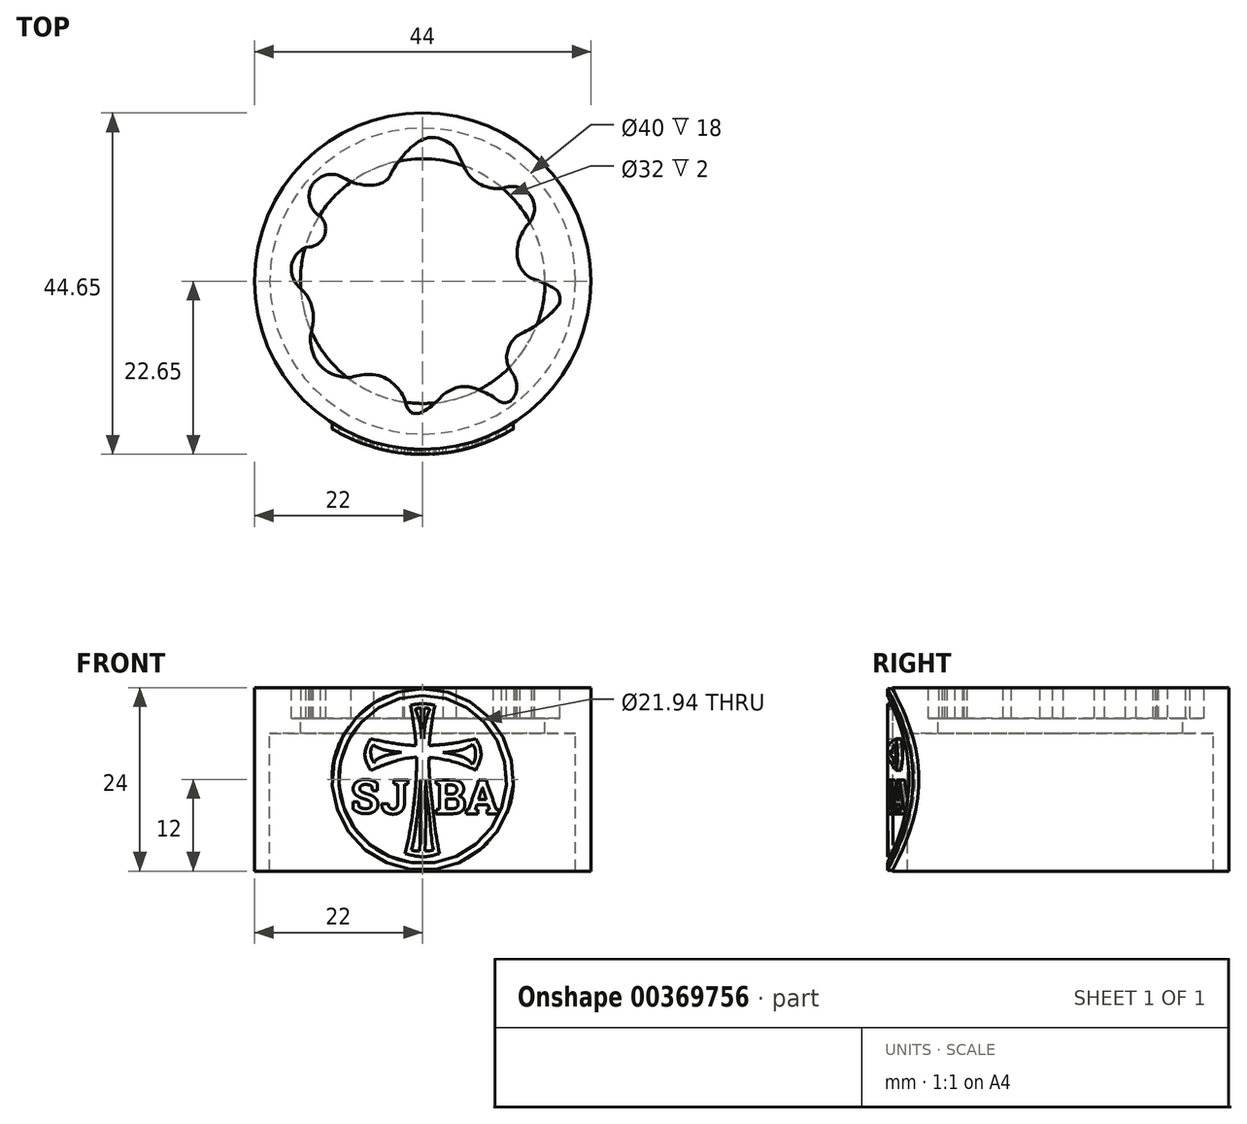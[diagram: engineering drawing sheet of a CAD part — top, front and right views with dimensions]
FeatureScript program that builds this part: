
annotation { "Feature Type Name" : "Feature", "Feature Type Description" : "" }
export const myFeature = defineFeature(function(context is Context, id is Id, definition is map)
    precondition{}
    {
        {
            var Q0;
            Q0=qCreatedBy(makeId("Top.planeOp"),FACE);
            var Q1;
            Q1=qBodyType(qCreatedBy(id+"F1",EDGE),BodyType.WIRE);
            cPlane(context, id + "F0", {"entities" : qUnion([Q0, Q1]), "cplaneType" : CPlaneType.OFFSET, "offset" : 12 * mm, "width" : 150 * mm, "height" : 150 * mm});
        }
        {
            var Q0;
            Q0=qCreatedBy(id+"F0.planeOp",FACE);
            var sketch = newSketch(context, id + "F1", { "sketchPlane" : qUnion([Q0])});
            skCircle(sketch, "E0", {"center": v(0, 0) * mm, "radius": 22 * mm});
            skFitSpline(sketch, "E1", {"points": [v(-14.3, 12.84) * mm, v(-11.44, 13.95) * mm, v(-6.4, 12.53) * mm], "startDerivative": vector(4.46, 5.6) * mm, "endDerivative": vector(16.32, 0.58) * mm});
            skFitSpline(sketch, "E2", {"points": [v(-14.3, 12.84) * mm, v(-14.8, 10.36) * mm, v(-13.38, 8.48) * mm], "startDerivative": vector(-2.91, -3.74) * mm, "endDerivative": vector(4.44, -2.3) * mm});
            skFitSpline(sketch, "E3", {"points": [v(-13.38, 8.48) * mm, v(-12.7, 6.62) * mm, v(-15.26, 4.45) * mm], "startDerivative": vector(2.5, -2.67) * mm, "endDerivative": vector(-9.07, 0.1) * mm});
            skFitSpline(sketch, "E4", {"points": [v(-15.26, 4.45) * mm, v(-17.17, 1.96) * mm, v(-15.87, -1.05) * mm], "startDerivative": vector(-5.88, -2.54) * mm, "endDerivative": vector(5.37, -3.99) * mm});
            skFitSpline(sketch, "E5", {"points": [v(-15.87, -1.05) * mm, v(-14.36, -3.98) * mm, v(-14.54, -6.45) * mm], "startDerivative": vector(4.6, -4.23) * mm, "endDerivative": vector(-1.12, -5.28) * mm});
            skFitSpline(sketch, "E6", {"points": [v(-14.54, -6.45) * mm, v(-14.3, -9.6) * mm, v(-9.38, -12.57) * mm], "startDerivative": vector(-1.49, -4.88) * mm, "endDerivative": vector(14.07, 0.6) * mm});
            skFitSpline(sketch, "E7", {"points": [v(-9.38, -12.57) * mm, v(-5.16, -12.57) * mm, v(-2.36, -15.43) * mm], "startDerivative": vector(7.18, 2.12) * mm, "endDerivative": vector(2.53, -6.19) * mm});
            skFitSpline(sketch, "E8", {"points": [v(-2.36, -15.43) * mm, v(-0.75, -17.32) * mm, v(2.7, -14.82) * mm], "startDerivative": vector(1.67, -9.42) * mm, "endDerivative": vector(5.03, 5.85) * mm});
            skFitSpline(sketch, "E9", {"points": [v(2.7, -14.82) * mm, v(5.45, -13.78) * mm, v(9.22, -15.14) * mm], "startDerivative": vector(4.06, 3.24) * mm, "endDerivative": vector(7.18, -3.93) * mm});
            skFitSpline(sketch, "E10", {"points": [v(9.22, -15.14) * mm, v(11.11, -15.85) * mm, v(12.13, -12.78) * mm], "startDerivative": vector(4.38, -3.77) * mm, "endDerivative": vector(-2.9, 8.35) * mm});
            skFitSpline(sketch, "E11", {"points": [v(12.13, -12.78) * mm, v(11.06, -10.66) * mm, v(11.96, -7.51) * mm], "startDerivative": vector(-1.65, 4.16) * mm, "endDerivative": vector(4.57, 5.25) * mm});
            skFitSpline(sketch, "E12", {"points": [v(11.96, -7.51) * mm, v(14.65, -5.88) * mm, v(17.91, -2.7) * mm], "startDerivative": vector(3.62, 3.57) * mm, "endDerivative": vector(-0.15, 3.1) * mm});
            skFitSpline(sketch, "E13", {"points": [v(17.91, -2.7) * mm, v(16.74, -0.7) * mm, v(14.28, 0.37) * mm], "startDerivative": vector(0.98, 7.59) * mm, "endDerivative": vector(-4.1, 1.2) * mm});
            skFitSpline(sketch, "E14", {"points": [v(14.28, 0.37) * mm, v(12.43, 2.83) * mm, v(12.74, 5.73) * mm], "startDerivative": vector(-6.41, 2.8) * mm, "endDerivative": vector(2.08, 5.38) * mm});
            skFitSpline(sketch, "E15", {"points": [v(12.74, 5.73) * mm, v(14.05, 7.73) * mm, v(14.57, 9.89) * mm], "startDerivative": vector(4.72, 10.1) * mm, "endDerivative": vector(-1.17, 4.74) * mm});
            skFitSpline(sketch, "E16", {"points": [v(14.57, 9.89) * mm, v(13.17, 12.02) * mm, v(10.32, 12.08) * mm], "startDerivative": vector(0.08, 3.85) * mm, "endDerivative": vector(-4.12, -2.28) * mm});
            skFitSpline(sketch, "E17", {"points": [v(10.32, 12.08) * mm, v(6.46, 13.4) * mm, v(4.44, 16.97) * mm], "startDerivative": vector(-9.93, -0.41) * mm, "endDerivative": vector(-5.62, 10.83) * mm});
            skFitSpline(sketch, "E18", {"points": [v(4.44, 16.97) * mm, v(1.52, 18.8) * mm, v(-2.58, 16.4) * mm], "startDerivative": vector(-2.9, 6.35) * mm, "endDerivative": vector(-8.38, -9.56) * mm});
            skFitSpline(sketch, "E19", {"points": [v(-2.58, 16.4) * mm, v(-4.36, 13.61) * mm, v(-6.4, 12.53) * mm], "startDerivative": vector(-9.43, -11.95) * mm, "endDerivative": vector(-8.2, -1.4) * mm});
            skCircle(sketch, "E20", {"center": v(0, 0) * mm, "radius": 20 * mm});
            skSolve(sketch);
        }
        {
            var Q0;
            Q0=qCreatedBy(makeId("Top.planeOp"),FACE);
            cPlane(context, id + "F2", {"entities" : qUnion([Q0]), "cplaneType" : CPlaneType.OFFSET, "offset" : 8 * mm, "width" : 150 * mm, "height" : 150 * mm});
        }
        {
            var Q0;
            Q0=qCreatedBy(id+"F2.planeOp",FACE);
            var sketch = newSketch(context, id + "F3", { "sketchPlane" : qUnion([Q0])});
            skCircle(sketch, "E21", {"center": v(0, 0) * mm, "radius": 20 * mm});
            skCircle(sketch, "E22", {"center": v(0, 0) * mm, "radius": 16 * mm});
            skSolve(sketch);
        }
        {
            var Q0;
            Q0=makeQuery(id+"F1.imprint","IMPRINT",FACE,{"disambiguationData":[TD([[makeQuery(id+"F1.imprint","IMPRINT",EDGE,{"derivedFrom":sQuery(id+"F1.wireOp",EDGE,"E1")}),1.0]])]});
            extrude(context, id + "F4", {"entities" : qUnion([Q0]), "oppositeDirection" : true, "depth" : 4 * mm});
        }
        {
            var Q0;
            Q0=makeQuery(id+"F1.imprint","IMPRINT",FACE,{"disambiguationData":[TD([[makeQuery(id+"F1.imprint","IMPRINT",EDGE,{"derivedFrom":sQuery(id+"F1.wireOp",EDGE,"E0")}),1.0]])]});
            extrude(context, id + "F5", {"entities" : qUnion([Q0]), "operationType" : NewBodyOperationType.ADD, "oppositeDirection" : true, "depth" : 24 * mm});
        }
        {
            var Q0;
            Q0=makeQuery(id+"F3.imprint","IMPRINT",FACE,{"disambiguationData":[TD([[makeQuery(id+"F3.imprint","IMPRINT",EDGE,{"derivedFrom":sQuery(id+"F3.wireOp",EDGE,"E21")}),1.0]])]});
            extrude(context, id + "F6", {"entities" : qUnion([Q0]), "operationType" : NewBodyOperationType.ADD, "oppositeDirection" : true, "depth" : 2 * mm});
        }
        {
            var Q0;
            Q0=qCreatedBy(id+"F0.planeOp",FACE);
            var sketch = newSketch(context, id + "F7", { "sketchPlane" : qUnion([Q0])});
            skCircle(sketch, "E23", {"center": v(0, 0) * mm, "radius": 22.65 * mm});
            skSolve(sketch);
        }
        {
            var Q0;
            Q0=qSketchRegion(id+"F7",true);
            var Q1;
            Q1=qConstructionFilter(qBodyType(qCreatedBy(id+"F7",EDGE),BodyType.WIRE),ConstructionObject.NO);
            extrude(context, id + "F8", {"entities" : qUnion([Q0]), "bodyType" : ToolBodyType.SURFACE, "operationType" : NewBodyOperationType.ADD, "surfaceEntities" : qUnion([Q1]), "oppositeDirection" : true, "depth" : 24 * mm});
        }
        {
            var Q0;
            Q0=qCreatedBy(makeId("Front.planeOp"),FACE);
            var sketch = newSketch(context, id + "F9", { "sketchPlane" : qUnion([Q0])});
            skCircle(sketch, "E24", {"center": v(0, 0) * mm, "radius": 11.87 * mm});
            skCircle(sketch, "E25", {"center": v(0, 0) * mm, "radius": 10.97 * mm});
            skFitSpline(sketch, "E26", {"points": [v(-1.6, 9.68) * mm, v(0, 9.89) * mm, v(1.61, 9.69) * mm], "startDerivative": vector(3.27, 0.75) * mm, "endDerivative": vector(4.3, -0.93) * mm});
            skFitSpline(sketch, "E27", {"points": [v(-0.95, 9.2) * mm, v(-0.62, 9.29) * mm, v(-0.24, 9.32) * mm], "startDerivative": vector(1.32, 0.5) * mm, "endDerivative": vector(1.3, -0.13) * mm});
            skFitSpline(sketch, "E28", {"points": [v(0.2, 9.33) * mm, v(0.57, 9.3) * mm, v(0.92, 9.18) * mm], "startDerivative": vector(0.76, -0.01) * mm, "endDerivative": vector(0.68, -0.27) * mm});
            skFitSpline(sketch, "E29", {"points": [v(-0.95, 9.2) * mm, v(-0.35, 7.32) * mm, v(-0.14, 5.33) * mm], "startDerivative": vector(1.4, -3.74) * mm, "endDerivative": vector(0.22, -4.02) * mm});
            skFitSpline(sketch, "E30", {"points": [v(-0.24, 9.32) * mm, v(-0.14, 7.25) * mm, v(-0.14, 5.33) * mm], "startDerivative": vector(0.55, -4.52) * mm, "endDerivative": vector(-0.28, -3.72) * mm});
            skFitSpline(sketch, "E31", {"points": [v(0.2, 9.33) * mm, v(0.11, 7.22) * mm, v(0.13, 5.32) * mm], "startDerivative": vector(-0.59, -4.52) * mm, "endDerivative": vector(0.33, -3.76) * mm});
            skFitSpline(sketch, "E32", {"points": [v(0.92, 9.18) * mm, v(0.34, 7.3) * mm, v(0.13, 5.32) * mm], "startDerivative": vector(-1.38, -3.36) * mm, "endDerivative": vector(-0.21, -3.99) * mm});
            skFitSpline(sketch, "E33", {"points": [v(-1.6, 9.68) * mm, v(-1.16, 7) * mm, v(-0.9, 4.42) * mm], "startDerivative": vector(1.25, -5.72) * mm, "endDerivative": vector(0.17, -4.96) * mm});
            skFitSpline(sketch, "E34", {"points": [v(1.61, 9.69) * mm, v(1.1, 6.86) * mm, v(0.85, 4.42) * mm], "startDerivative": vector(-1.57, -6.3) * mm, "endDerivative": vector(-0.19, -5) * mm});
            skFitSpline(sketch, "E35", {"points": [v(0.85, 4.42) * mm, v(3.78, 4.7) * mm, v(6.94, 5.32) * mm], "startDerivative": vector(5.94, 0.4) * mm, "endDerivative": vector(6.24, 1.38) * mm});
            skFitSpline(sketch, "E36", {"points": [v(6.94, 5.32) * mm, v(7.64, 3.38) * mm, v(6.94, 1.21) * mm], "startDerivative": vector(2.1, -3.9) * mm, "endDerivative": vector(-2.07, -4.3) * mm});
            skFitSpline(sketch, "E37", {"points": [v(6.94, 1.21) * mm, v(3.65, 2.41) * mm, v(0.84, 2.9) * mm], "startDerivative": vector(-6.35, 2.62) * mm, "endDerivative": vector(-5.85, 0.72) * mm});
            skFitSpline(sketch, "E38", {"points": [v(-0.9, 4.42) * mm, v(-3.84, 4.73) * mm, v(-6.81, 5.3) * mm], "startDerivative": vector(-6.82, 0.08) * mm, "endDerivative": vector(-5.92, 1.3) * mm});
            skFitSpline(sketch, "E39", {"points": [v(-6.81, 5.3) * mm, v(-7.57, 3.31) * mm, v(-6.81, 1.17) * mm], "startDerivative": vector(-2.27, -4.02) * mm, "endDerivative": vector(2.25, -4.25) * mm});
            skFitSpline(sketch, "E40", {"points": [v(-6.81, 1.17) * mm, v(-3.87, 2.3) * mm, v(-0.79, 2.9) * mm], "startDerivative": vector(5.8, 2.52) * mm, "endDerivative": vector(6.2, 0.13) * mm});
            skFitSpline(sketch, "E41", {"points": [v(-0.79, 2.9) * mm, v(-1.18, -3.52) * mm, v(-2.3, -9.7) * mm], "startDerivative": vector(0.03, -12.8) * mm, "endDerivative": vector(-3.05, -12.4) * mm});
            skFitSpline(sketch, "E42", {"points": [v(0.84, 2.9) * mm, v(1.3, -3.5) * mm, v(2.2, -9.72) * mm], "startDerivative": vector(-0.69, -12.85) * mm, "endDerivative": vector(2.87, -12.23) * mm});
            skFitSpline(sketch, "E43", {"points": [v(-2.3, -9.7) * mm, v(0, -10.11) * mm, v(2.2, -9.72) * mm], "startDerivative": vector(4.57, -1.2) * mm, "endDerivative": vector(4.44, 1.2) * mm});
            skFitSpline(sketch, "E44", {"points": [v(-0.31, -0.15) * mm, v(-0.77, -5.17) * mm, v(-1.46, -9.24) * mm], "startDerivative": vector(-0.44, -9.93) * mm, "endDerivative": vector(-2.1, -8.23) * mm});
            skFitSpline(sketch, "E45", {"points": [v(-0.31, -0.15) * mm, v(-0.31, -5.21) * mm, v(-0.4, -9.39) * mm], "startDerivative": vector(0.34, -10.34) * mm, "endDerivative": vector(-0.5, -8.7) * mm});
            skFitSpline(sketch, "E46", {"points": [v(-1.46, -9.24) * mm, v(-0.92, -9.37) * mm, v(-0.4, -9.39) * mm], "startDerivative": vector(1.08, -0.3) * mm, "endDerivative": vector(1.05, 0.02) * mm});
            skFitSpline(sketch, "E47", {"points": [v(0.4, -0.18) * mm, v(0.94, -5.12) * mm, v(1.4, -9.22) * mm], "startDerivative": vector(0.4, -9.84) * mm, "endDerivative": vector(1.98, -8.22) * mm});
            skFitSpline(sketch, "E48", {"points": [v(0.4, -0.18) * mm, v(0.4, -5.14) * mm, v(0.31, -9.34) * mm], "startDerivative": vector(-0.8, -13.59) * mm, "endDerivative": vector(-0.1, -10.76) * mm});
            skFitSpline(sketch, "E49", {"points": [v(-6.43, 4.51) * mm, v(-6.8, 3.41) * mm, v(-6.36, 2.16) * mm], "startDerivative": vector(-2.23, -2.18) * mm, "endDerivative": vector(1.7, -2.44) * mm});
            skFitSpline(sketch, "E50", {"points": [v(-6.43, 4.51) * mm, v(-5.01, 3.85) * mm, v(-2.77, 3.54) * mm], "startDerivative": vector(3.18, -2.63) * mm, "endDerivative": vector(4.45, -0.3) * mm});
            skFitSpline(sketch, "E51", {"points": [v(-6.36, 2.16) * mm, v(-5.08, 3.04) * mm, v(-2.77, 3.54) * mm], "startDerivative": vector(1.7, 3.32) * mm, "endDerivative": vector(4.67, 0.59) * mm});
            skFitSpline(sketch, "E52", {"points": [v(2.66, 3.52) * mm, v(4.86, 3.8) * mm, v(6.5, 4.6) * mm], "startDerivative": vector(4.4, 0.25) * mm, "endDerivative": vector(2.66, 2.4) * mm});
            skFitSpline(sketch, "E53", {"points": [v(2.66, 3.52) * mm, v(4.87, 3.06) * mm, v(6.51, 1.95) * mm], "startDerivative": vector(4.52, -0.54) * mm, "endDerivative": vector(2.8, -3.96) * mm});
            skFitSpline(sketch, "E54", {"points": [v(6.5, 4.6) * mm, v(6.9, 3.27) * mm, v(6.51, 1.95) * mm], "startDerivative": vector(2.04, -2.66) * mm, "endDerivative": vector(-1.92, -2.43) * mm});
            skFitSpline(sketch, "E55", {"points": [v(0.31, -9.34) * mm, v(0.9, -9.34) * mm, v(1.4, -9.22) * mm], "startDerivative": vector(1.15, -0.06) * mm, "endDerivative": vector(1.03, 0.3) * mm});
            skSolve(sketch);
        }
        {
            var Q0;
            Q0=qCreatedBy(makeId("Front.planeOp"),FACE);
            var sketch = newSketch(context, id + "F10", { "sketchPlane" : qUnion([Q0])});
            skText(sketch, "E56", { "text": "S", "fontName": "RobotoSlab-Bold.ttf"});
            skText(sketch, "E57", { "text": "J", "fontName": "RobotoSlab-Bold.ttf"});
            skText(sketch, "E58", { "text": "B", "fontName": "RobotoSlab-Bold.ttf"});
            skText(sketch, "E59", { "text": "A", "fontName": "RobotoSlab-Bold.ttf"});
            const initialGuessF10  = {"E56": [-0.0094, -0.00443, 1, 0, 0.00443], "E57": [-0.00546, -0.0045, 1, 0, 0.0045], "E58": [0.00155, -0.0045, 1, 0, 0.0045], "E59": [0.00556, -0.0045, 1, 0, 0.0045]};
            skSetInitialGuess(sketch, initialGuessF10);
            skSolve(sketch);
        }
        {
            var Q0;
            Q0=makeQuery(id+"F9.imprint","IMPRINT",FACE,{"disambiguationData":[TD([[makeQuery(id+"F9.imprint","IMPRINT",EDGE,{"derivedFrom":sQuery(id+"F9.wireOp",EDGE,"E24")}),1.0]])]});
            var Q1;
            Q1=makeQuery(id+"F9.imprint","IMPRINT",FACE,{"disambiguationData":[TD([[makeQuery(id+"F9.imprint","IMPRINT",EDGE,{"derivedFrom":sQuery(id+"F9.wireOp",EDGE,"E26")}),-1.0]])]});
            var Q2;
            Q2 = qSketchRegion(id + "F10", true);
            var Q3;
            Q3=makeQuery(id+"F8.opExtrude","SWEPT_FACE",FACE,{"disambiguationData":[OSD([sQuery(id+"F7.wireOp",EDGE,"E23")])]});
            var Q4;
            Q4=makeQuery(id+"F5.opExtrude","SWEPT_FACE",FACE,{"disambiguationData":[OSD([sQuery(id+"F1.wireOp",EDGE,"E0")])]});
            extrude(context, id + "F11", {"entities" : qUnion([Q0, Q1, Q2]), "operationType" : NewBodyOperationType.ADD, "endBound" : BoundingType.UP_TO_SURFACE, "endBoundEntityFace" : qUnion([Q3]), "depth" : 25 * mm, "hasSecondDirection" : true, "secondDirectionBound" : SecondDirectionBoundingType.UP_TO_SURFACE, "secondDirectionOppositeDirection" : false, "secondDirectionBoundEntityFace" : qUnion([Q4]), "secondDirectionDepth" : 25 * mm, "offsetDistance" : 25 * mm});
        }
    });
